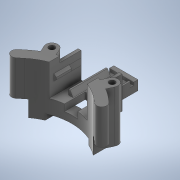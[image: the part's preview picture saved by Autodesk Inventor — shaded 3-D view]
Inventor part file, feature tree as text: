
AUTODESK INVENTOR PART (.ipt)
format: ipt  version: 2020 (Build 240168000, 168)  size: 709,120 bytes
history: native  units: mm
features: extrude x19, sketch x18, projected_geometry x16, other x5, sweep x1, chamfer x1
ambient origin geometry x8: Origin, YZ Plane, XZ Plane, XY Plane, X Axis, Y Axis, Z Axis, Center Point
bodies: Body1 (feature_tree)
feature tree (60):
  other  "Твердое тело1"
  extrude  "Выдавливание1"  Depth=35.0mm TaperAngle=0.0deg
  sketch  "Эскиз2"
  extrude  "Выдавливание2"  Depth=4.0mm
  sweep  "Сдвиг1"
  extrude  "Выдавливание5"  Depth=8.0mm
  extrude  "Выдавливание6"  Depth=35.0mm TaperAngle=0.0deg
  extrude  "Выдавливание7"  Depth=8.5mm
  extrude  "Выдавливание8"  TaperAngle=45.0deg  [1 undecoded]
  other  "РабПлоскость1"
  extrude  "Выдавливание9"  Depth=8.5mm
  extrude  "Выдавливание10"  TaperAngle=45.0deg  [1 undecoded]
  extrude  "Выдавливание11"  TaperAngle=0.0deg  [1 undecoded]
  sketch  "Эскиз13"
  other  "РабПлоскость2"
  sketch  "Эскиз14"
  extrude  "Выдавливание12"  Depth=5.0mm TaperAngle=0.0deg
  extrude  "Выдавливание13"  Depth=15.0mm TaperAngle=0.0deg
  other  "РабПлоскость3"
  extrude  "Выдавливание14"  Depth=15.0mm TaperAngle=0.0deg
  extrude  "Выдавливание15"  Depth=26.0mm
  extrude  "Выдавливание16"  Depth=6.0mm
  extrude  "Выдавливание17"  Depth=15.0mm TaperAngle=0.0deg
  chamfer  "Фаска1"  Distance=2.0mm
  other  "РабПлоскость4"
  sketch  "Эскиз18"
  extrude  "Выдавливание18"  Depth=1.5mm
  extrude  "Выдавливание19"  Depth=3.0mm
  extrude  "Выдавливание20"  Depth=6.0mm
  extrude  "Выдавливание21"  Depth=3.5mm TaperAngle=0.0deg
  sketch  "Эскиз1"
  sketch  "Эскиз3"
  projected_geometry  "Спроецированная петля1"
  projected_geometry  "Спроецированная петля2"
  sketch  "3D эскиз1"
  sketch  "Эскиз4"
  sketch  "Эскиз6"
  projected_geometry  "Спроецированная петля4"
  sketch  "Эскиз7"
  projected_geometry  "Спроецированная петля5"
  sketch  "Эскиз9"
  projected_geometry  "Спроецированная петля7"
  sketch  "Эскиз11"
  projected_geometry  "Спроецированная петля8"
  sketch  "Эскиз12"
  projected_geometry  "Спроецированная петля9"
  projected_geometry  "Спроецированная петля10"
  sketch  "Эскиз15"
  sketch  "Эскиз16"
  projected_geometry  "Спроецированная петля11"
  projected_geometry  "Спроецированная петля12"
  sketch  "Эскиз17"
  projected_geometry  "Спроецированная петля13"
  projected_geometry  "Спроецированная петля14"
  projected_geometry  "Спроецированная петля15"
  projected_geometry  "Спроецированная петля16"
  sketch  "Эскиз19"
  projected_geometry  "Спроецированная петля17"
  projected_geometry  "Спроецированная петля18"
  sketch  "Эскиз20"
note: 3 required parameter values undecoded (feature->parameter linkage not recoverable at this tier; creation-order binding heuristic only, values carry confidence <= 0.55)
